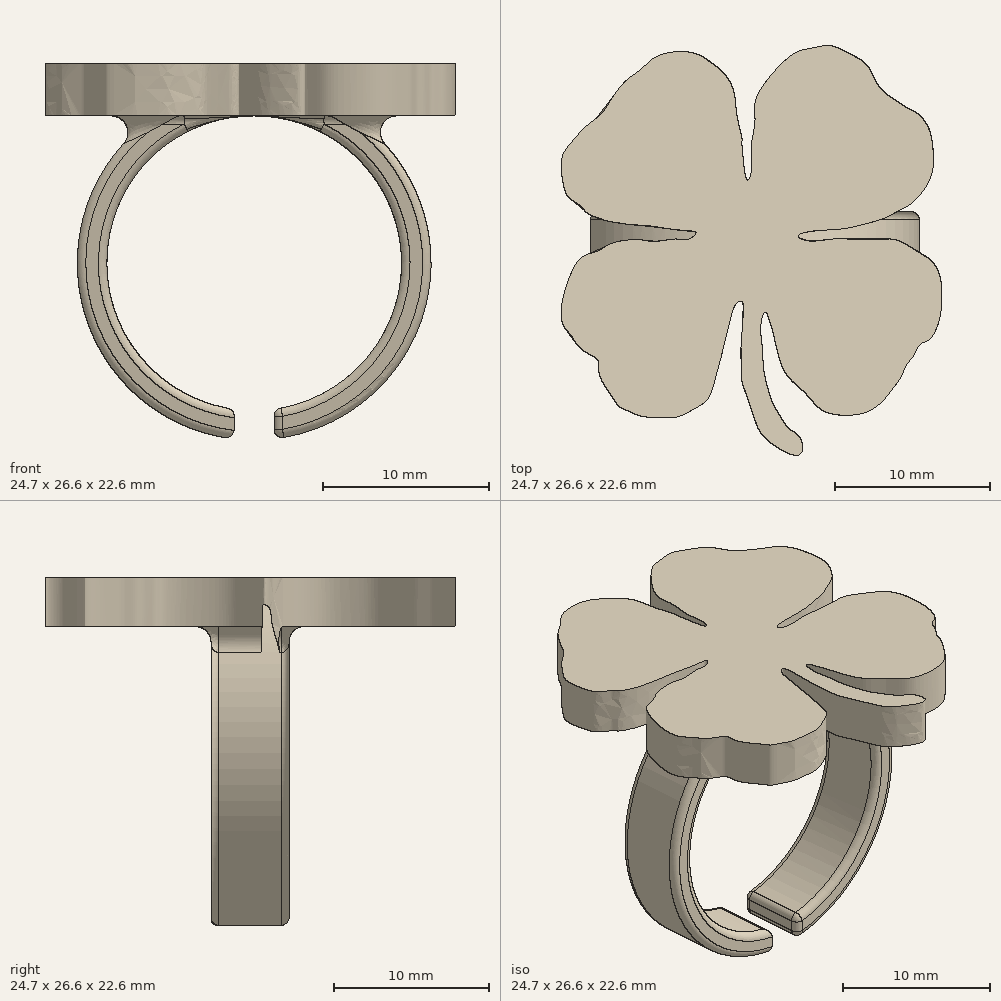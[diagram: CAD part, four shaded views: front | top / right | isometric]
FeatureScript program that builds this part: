
annotation { "Feature Type Name" : "Feature", "Feature Type Description" : "" }
export const myFeature = defineFeature(function(context is Context, id is Id, definition is map)
    precondition{}
    {
        {
            var Q0;
            Q0=qCreatedBy(makeId("Top.planeOp"),FACE);
            var sketch = newSketch(context, id + "F0", { "sketchPlane" : qUnion([Q0])});
            skLineSegment(sketch, "E0.bottom", {"start": v(-12.7, 13.55) * mm, "end": v(12.7, 13.55) * mm});
            skLineSegment(sketch, "E0.top", {"start": v(-12.7, -13.55) * mm, "end": v(12.7, -13.55) * mm, "construction": true});
            skLineSegment(sketch, "E0.left", {"start": v(-12.7, 13.55) * mm, "end": v(-12.7, -13.55) * mm, "construction": true});
            skLineSegment(sketch, "E0.right", {"start": v(12.7, 13.55) * mm, "end": v(12.7, -13.55) * mm, "construction": true});
            skLineSegment(sketch, "E1", {"start": v(-12.7, 13.55) * mm, "end": v(0, 0) * mm, "construction": true});
            skLineSegment(sketch, "E2", {"start": v(0, 0) * mm, "end": v(12.7, 13.55) * mm, "construction": true});
            skLineSegment(sketch, "E3", {"start": v(0, 0) * mm, "end": v(12.7, -13.55) * mm, "construction": true});
            skFitSpline(sketch, "E4", {"points": [v(2.93, -13.23) * mm, v(1.1, -12.53) * mm, v(0.23, -11.56) * mm, v(-0.26, -10.22) * mm, v(-0.8, -8.62) * mm, v(-0.87, -8.1) * mm, v(-0.92, -6.49) * mm, v(-0.9, -6.14) * mm, v(-0.76, -4.58) * mm, v(-0.87, -3.28) * mm, v(-1.29, -3.56) * mm, v(-1.64, -4.7) * mm, v(-2.04, -6.2) * mm, v(-2.15, -6.73) * mm, v(-2.43, -7.76) * mm, v(-2.76, -9.01) * mm, v(-3.16, -9.76) * mm, v(-3.88, -10.25) * mm, v(-5.1, -10.8) * mm, v(-6.4, -10.82) * mm, v(-6.96, -10.8) * mm, v(-7.57, -10.68) * mm, v(-8.01, -10.49) * mm, v(-8.83, -10.11) * mm, v(-9.07, -9.78) * mm, v(-10.1, -8.03) * mm, v(-10.19, -7.15) * mm, v(-10.85, -6.66) * mm, v(-11.16, -6.47) * mm, v(-11.64, -5.98) * mm, v(-11.88, -5.56) * mm, v(-12.5, -4.7) * mm, v(-12.38, -2.77) * mm, v(-11.86, -1.32) * mm, v(-11.15, -0.37) * mm, v(-10.14, 0) * mm, v(-9.22, 0.5) * mm, v(-7.29, 0.7) * mm, v(-6.56, 0.6) * mm, v(-5.05, 0.77) * mm, v(-4.28, 0.75) * mm, v(-3.81, 1.17) * mm, v(-4.6, 1.32) * mm, v(-6.01, 1.5) * mm, v(-6.72, 1.6) * mm, v(-7.97, 1.7) * mm, v(-9.57, 1.93) * mm, v(-10.01, 2.07) * mm, v(-10.93, 2.48) * mm, v(-11.26, 2.86) * mm, v(-12.08, 3.45) * mm, v(-12.47, 4.47) * mm, v(-12.52, 6.07) * mm, v(-11.88, 7.06) * mm, v(-10.96, 8.07) * mm, v(-10.08, 8.75) * mm, v(-9.72, 9.17) * mm, v(-9.27, 9.89) * mm, v(-8.36, 11.04) * mm, v(-7.37, 11.78) * mm, v(-6.52, 12.53) * mm, v(-5.1, 12.93) * mm, v(-3.75, 12.77) * mm, v(-2.7, 12.11) * mm, v(-1.95, 11.45) * mm, v(-1.37, 10.35) * mm, v(-1.18, 8.82) * mm, v(-0.85, 7.34) * mm, v(-0.85, 7) * mm, v(-0.72, 5.45) * mm, v(-0.47, 4.58) * mm, v(-0.2, 5.28) * mm, v(-0.25, 6.66) * mm, v(0, 8.33) * mm, v(0, 9.59) * mm, v(0.67, 10.9) * mm, v(1.92, 12.31) * mm, v(2.89, 12.97) * mm, v(3.86, 13.19) * mm, v(4.89, 13.32) * mm, v(6.1, 12.84) * mm, v(7.24, 12.1) * mm, v(7.86, 11.01) * mm, v(8.38, 10.31) * mm, v(9.15, 9.76) * mm, v(9.85, 9.3) * mm, v(10.6, 8.88) * mm, v(11.24, 8.05) * mm, v(11.5, 7.08) * mm, v(11.57, 5.41) * mm, v(11.1, 4.14) * mm, v(10.27, 3.15) * mm, v(9.5, 2.66) * mm, v(8.36, 2.1) * mm, v(7.33, 1.78) * mm, v(5.75, 1.43) * mm, v(3.68, 1.28) * mm, v(2.82, 0.95) * mm, v(3.53, 0.64) * mm, v(5.15, 0.77) * mm, v(7.54, 0.72) * mm, v(9.13, 0.72) * mm, v(10.5, 0) * mm, v(11.53, -0.72) * mm, v(12.08, -2.02) * mm, v(12.05, -4.15) * mm, v(11.78, -5.07) * mm, v(11.32, -5.78) * mm, v(10.75, -6.08) * mm, v(10.31, -6.83) * mm, v(9.85, -7.42) * mm, v(9.52, -8.17) * mm, v(9.08, -8.8) * mm, v(8.46, -9.6) * mm, v(7.67, -10.28) * mm, v(6.66, -10.63) * mm, v(4.9, -10.57) * mm, v(4, -10.06) * mm, v(3.23, -9.2) * mm, v(2.2, -8.24) * mm, v(1.6, -7.1) * mm, v(1.3, -5.8) * mm, v(0.95, -4.55) * mm, v(0.66, -3.97) * mm, v(0.38, -4.92) * mm, v(0.49, -6.37) * mm, v(0.55, -7.67) * mm, v(0.9, -9.16) * mm, v(1.15, -9.89) * mm, v(1.48, -10.46) * mm, v(2.03, -11.34) * mm, v(2.42, -11.69) * mm, v(2.97, -12.21) * mm, v(2.93, -13.23) * mm]});
            skSolve(sketch);
        }
        {
            var Q0;
            Q0 = qSketchRegion(id + "F0", true);
            extrude(context, id + "F1", {"entities" : qUnion([Q0]), "depth" : 3.17 * mm, "offsetDistance" : 25.4 * mm});
        }
        {
            var Q0;
            Q0=makeQuery(id+"F1.opExtrude","CAP_FACE",FACE,{"disambiguationData":[OSD([sQuery(id+"F0.wireOp",EDGE,"E4")])],"isStart":false});
            var sketch = newSketch(context, id + "F2", { "sketchPlane" : qUnion([Q0])});
            skSolve(sketch);
        }
        {
            var Q0;
            Q0=qCreatedBy(makeId("Front.planeOp"),FACE);
            var sketch = newSketch(context, id + "F3", { "sketchPlane" : qUnion([Q0])});
            skCircle(sketch, "E5", {"center": v(0, -8.9) * mm, "radius": 10.67 * mm});
            skCircle(sketch, "E6", {"center": v(0, -8.9) * mm, "radius": 8.9 * mm});
            skSolve(sketch);
        }
        {
            var Q0;
            Q0 = qSketchRegion(id + "F3", true);
            extrude(context, id + "F4", {"entities" : qUnion([Q0]), "operationType" : NewBodyOperationType.ADD, "endBound" : BoundingType.SYMMETRIC, "depth" : 5.08 * mm, "offsetDistance" : 25.4 * mm});
        }
        {
            var Q0;
            Q0=makeQuery(id+"F4.opExtrude","CAP_FACE",FACE,{"disambiguationData":[OSD([sQuery(id+"F3.wireOp",EDGE,"E5"),sQuery(id+"F3.wireOp",EDGE,"E6")])],"isStart":false});
            var sketch = newSketch(context, id + "F5", { "sketchPlane" : qUnion([Q0])});
            skLineSegment(sketch, "E7.bottom", {"start": v(-1.2, -8.25) * mm, "end": v(1.2, -8.25) * mm});
            skLineSegment(sketch, "E7.top", {"start": v(-1.2, -22.58) * mm, "end": v(1.2, -22.58) * mm});
            skLineSegment(sketch, "E7.left", {"start": v(-1.2, -8.25) * mm, "end": v(-1.2, -22.58) * mm});
            skLineSegment(sketch, "E7.right", {"start": v(1.2, -8.25) * mm, "end": v(1.2, -22.58) * mm});
            skLineSegment(sketch, "E8", {"start": v(-1.2, -8.25) * mm, "end": v(0, -8.89) * mm});
            skLineSegment(sketch, "E9", {"start": v(0, -8.89) * mm, "end": v(1.2, -8.25) * mm});
            skSolve(sketch);
        }
        {
            var Q0;
            Q0 = qSketchRegion(id + "F5", true);
            extrude(context, id + "F6", {"entities" : qUnion([Q0]), "operationType" : NewBodyOperationType.REMOVE, "oppositeDirection" : true, "depth" : 25.4 * mm, "offsetDistance" : 25.4 * mm});
        }
        {
            var Q0;
            Q0=makeQuery(id+"F2.imprint","IMPRINT",FACE,{"disambiguationData":[TD([[makeQuery(id+"F2.imprint","IMPRINT",EDGE,{"derivedFrom":makeQuery(id+"F1.opExtrude","CAP_EDGE",EDGE,{"disambiguationData":[OSD([sQuery(id+"F0.wireOp",EDGE,"E4")])],"isStart":false})}),-1.0]])]});
            var sketch = newSketch(context, id + "F7", { "sketchPlane" : qUnion([Q0])});
            skText(sketch, "E10", { "text": "CL", "fontName": "OpenSans-Bold.ttf"});
            const initialGuessF7  = {"E10": [-0.00423, -0.00215, 1, 0, 0.00567]};
            skSetInitialGuess(sketch, initialGuessF7);
            skSolve(sketch);
        }
        {
            var Q0;
            Q0=makeQuery(id+"F6.boolean.opBoolean","INTERSECT",EDGE,{"derivedFrom":[makeQuery(id+"F4.opExtrude","SWEPT_FACE",FACE,{"disambiguationData":[OSD([sQuery(id+"F3.wireOp",EDGE,"E6")])]}),makeQuery(id+"F6.opExtrude","SWEPT_FACE",FACE,{"disambiguationData":[OSD([sQuery(id+"F5.wireOp",EDGE,"E7.right")])]})]});
            var Q1;
            Q1=makeQuery(id+"F6.boolean.opBoolean","INTERSECT",EDGE,{"derivedFrom":[makeQuery(id+"F4.opExtrude","SWEPT_FACE",FACE,{"disambiguationData":[OSD([sQuery(id+"F3.wireOp",EDGE,"E6")])]}),makeQuery(id+"F6.opExtrude","SWEPT_FACE",FACE,{"disambiguationData":[OSD([sQuery(id+"F5.wireOp",EDGE,"E7.left")])]})]});
            var Q2;
            Q2=makeQuery(id+"F6.boolean.opBoolean","INTERSECT",EDGE,{"derivedFrom":[makeQuery(id+"F4.opExtrude","SWEPT_FACE",FACE,{"disambiguationData":[OSD([sQuery(id+"F3.wireOp",EDGE,"E5")])]}),makeQuery(id+"F6.opExtrude","SWEPT_FACE",FACE,{"disambiguationData":[OSD([sQuery(id+"F5.wireOp",EDGE,"E7.right")])]})]});
            var Q3;
            Q3=makeQuery(id+"F6.boolean.opBoolean","INTERSECT",EDGE,{"derivedFrom":[makeQuery(id+"F4.opExtrude","SWEPT_FACE",FACE,{"disambiguationData":[OSD([sQuery(id+"F3.wireOp",EDGE,"E5")])]}),makeQuery(id+"F6.opExtrude","SWEPT_FACE",FACE,{"disambiguationData":[OSD([sQuery(id+"F5.wireOp",EDGE,"E7.left")])]})]});
            var Q4;
            {var subQ0=sQuery(id+"F3.wireOp",EDGE,"E5");Q4=makeQuery(id+"F6.boolean.opBoolean","SPLIT",EDGE,{"disambiguationData":[TD([makeQuery(id+"F6.opExtrude","SWEPT_FACE",FACE,{"disambiguationData":[OSD([sQuery(id+"F5.wireOp",EDGE,"E7.left")])]})])],"derivedFrom":makeQuery(id+"F4.opExtrude","CAP_EDGE",EDGE,{"disambiguationData":[OSD([subQ0])],"isStart":true})});}
            var Q5;
            {var subQ0=sQuery(id+"F3.wireOp",EDGE,"E6");Q5=makeQuery(id+"F6.boolean.opBoolean","SPLIT",EDGE,{"disambiguationData":[TD([makeQuery(id+"F6.opExtrude","SWEPT_FACE",FACE,{"disambiguationData":[OSD([sQuery(id+"F5.wireOp",EDGE,"E7.left")])]})])],"derivedFrom":makeQuery(id+"F4.opExtrude","CAP_EDGE",EDGE,{"disambiguationData":[OSD([subQ0])],"isStart":true})});}
            var Q6;
            {var subQ0=sQuery(id+"F3.wireOp",EDGE,"E5");Q6=makeQuery(id+"F6.boolean.opBoolean","SPLIT",EDGE,{"disambiguationData":[TD([makeQuery(id+"F6.opExtrude","SWEPT_FACE",FACE,{"disambiguationData":[OSD([sQuery(id+"F5.wireOp",EDGE,"E7.left")])]})])],"derivedFrom":makeQuery(id+"F4.opExtrude","CAP_EDGE",EDGE,{"disambiguationData":[OSD([subQ0])],"isStart":false})});}
            var Q7;
            {var subQ0=sQuery(id+"F3.wireOp",EDGE,"E6");Q7=makeQuery(id+"F6.boolean.opBoolean","SPLIT",EDGE,{"disambiguationData":[TD([makeQuery(id+"F6.opExtrude","SWEPT_FACE",FACE,{"disambiguationData":[OSD([sQuery(id+"F5.wireOp",EDGE,"E7.left")])]})])],"derivedFrom":makeQuery(id+"F4.opExtrude","CAP_EDGE",EDGE,{"disambiguationData":[OSD([subQ0])],"isStart":false})});}
            var Q8;
            {var subQ0=sQuery(id+"F3.wireOp",EDGE,"E6");var subQ1=sQuery(id+"F3.wireOp",EDGE,"E5");var subQ2=makeQuery(id+"F4.opExtrude","CAP_FACE",FACE,{"disambiguationData":[OSD([subQ1,subQ0])],"isStart":false});Q8=makeQuery(id+"F6.boolean.opBoolean","SPLIT",FACE,{"disambiguationData":[TD([makeQuery(id+"F6.opExtrude","SWEPT_FACE",FACE,{"disambiguationData":[OSD([sQuery(id+"F5.wireOp",EDGE,"E7.right")])]})])],"derivedFrom":subQ2});}
            var Q9;
            {var subQ0=sQuery(id+"F3.wireOp",EDGE,"E5");Q9=makeQuery(id+"F6.boolean.opBoolean","SPLIT",EDGE,{"disambiguationData":[TD([makeQuery(id+"F6.opExtrude","SWEPT_FACE",FACE,{"disambiguationData":[OSD([sQuery(id+"F5.wireOp",EDGE,"E7.right")])]})])],"derivedFrom":makeQuery(id+"F4.opExtrude","CAP_EDGE",EDGE,{"disambiguationData":[OSD([subQ0])],"isStart":true})});}
            var Q10;
            Q10=makeQuery(id+"F6.boolean.opBoolean","INTERSECT",EDGE,{"derivedFrom":[makeQuery(id+"F4.opExtrude","CAP_FACE",FACE,{"disambiguationData":[OSD([sQuery(id+"F3.wireOp",EDGE,"E5"),sQuery(id+"F3.wireOp",EDGE,"E6")])],"isStart":true}),makeQuery(id+"F6.opExtrude","SWEPT_FACE",FACE,{"disambiguationData":[OSD([sQuery(id+"F5.wireOp",EDGE,"E7.left")])]})]});
            var Q11;
            Q11=makeQuery(id+"F6.boolean.opBoolean","INTERSECT",EDGE,{"derivedFrom":[makeQuery(id+"F4.opExtrude","CAP_FACE",FACE,{"disambiguationData":[OSD([sQuery(id+"F3.wireOp",EDGE,"E5"),sQuery(id+"F3.wireOp",EDGE,"E6")])],"isStart":true}),makeQuery(id+"F6.opExtrude","SWEPT_FACE",FACE,{"disambiguationData":[OSD([sQuery(id+"F5.wireOp",EDGE,"E7.right")])]})]});
            var Q12;
            Q12=makeQuery(id+"F6.boolean.opBoolean","COPY",EDGE,{"derivedFrom":makeQuery(id+"F6.opExtrude","CAP_EDGE",EDGE,{"disambiguationData":[OSD([sQuery(id+"F5.wireOp",EDGE,"E7.left")])],"isStart":true})});
            fillet(context, id + "F8", {"entities" : qUnion([Q0, Q1, Q2, Q3, Q4, Q5, Q6, Q7, Q8, Q9, Q10, Q11, Q12]), "radius" : 0.5 * mm, "tangentPropagation" : true, "allowEdgeOverflow" : false});
        }
        {
            var Q0;
            Q0=makeQuery(id+"F4.boolean.opBoolean","INTERSECT",EDGE,{"disambiguationData":[OD(1.0)],"derivedFrom":[makeQuery(id+"F1.opExtrude","CAP_FACE",FACE,{"disambiguationData":[OSD([sQuery(id+"F0.wireOp",EDGE,"E4")])],"isStart":true}),makeQuery(id+"F4.opExtrude","SWEPT_FACE",FACE,{"disambiguationData":[OSD([sQuery(id+"F3.wireOp",EDGE,"E5")])]})]});
            var Q1;
            Q1=makeQuery(id+"F4.boolean.opBoolean","INTERSECT",EDGE,{"disambiguationData":[OD(2.0)],"derivedFrom":[makeQuery(id+"F1.opExtrude","CAP_FACE",FACE,{"disambiguationData":[OSD([sQuery(id+"F0.wireOp",EDGE,"E4")])],"isStart":true}),makeQuery(id+"F4.opExtrude","SWEPT_FACE",FACE,{"disambiguationData":[OSD([sQuery(id+"F3.wireOp",EDGE,"E5")])]})]});
            var Q2;
            Q2=makeQuery(id+"F4.boolean.opBoolean","INTERSECT",EDGE,{"disambiguationData":[OD(0.0)],"derivedFrom":[makeQuery(id+"F1.opExtrude","CAP_FACE",FACE,{"disambiguationData":[OSD([sQuery(id+"F0.wireOp",EDGE,"E4")])],"isStart":true}),makeQuery(id+"F4.opExtrude","SWEPT_FACE",FACE,{"disambiguationData":[OSD([sQuery(id+"F3.wireOp",EDGE,"E5")])]})]});
            fillet(context, id + "F9", {"entities" : qUnion([Q0, Q1, Q2]), "radius" : 1.02 * mm, "tangentPropagation" : true, "allowEdgeOverflow" : false});
        }
    });
